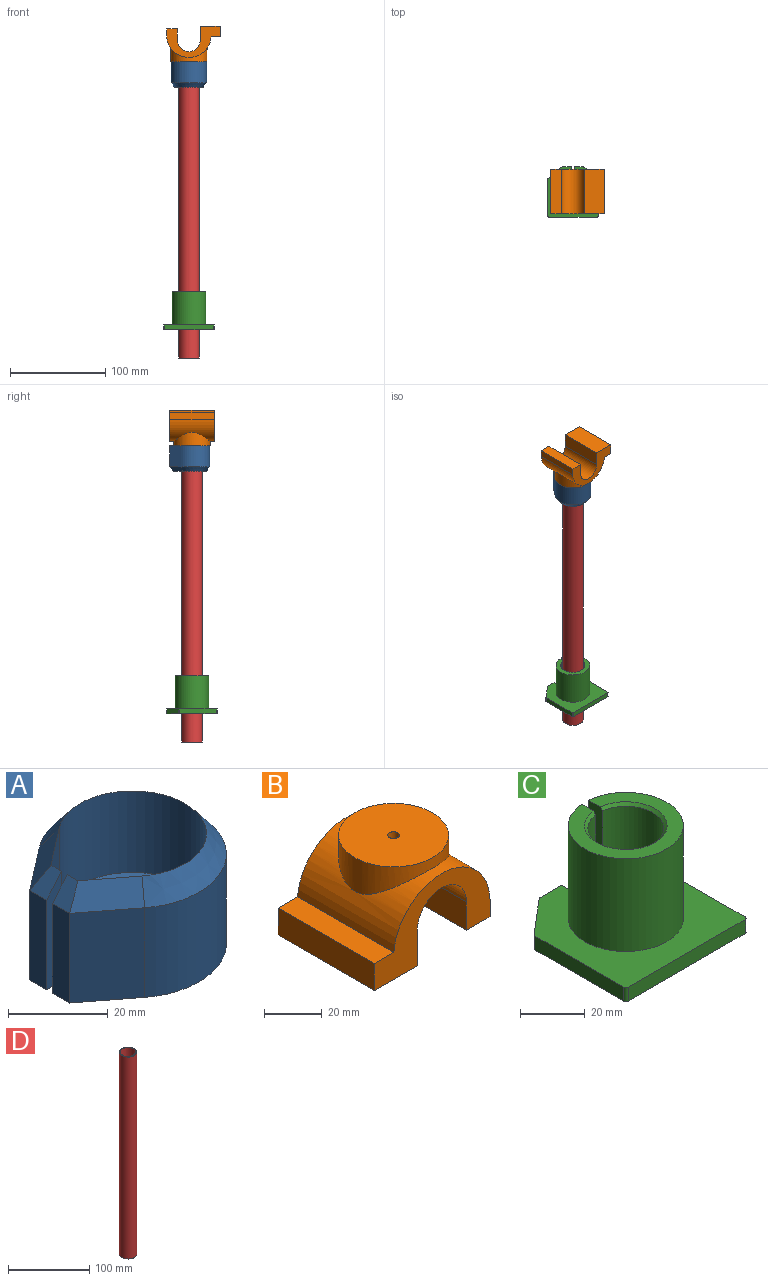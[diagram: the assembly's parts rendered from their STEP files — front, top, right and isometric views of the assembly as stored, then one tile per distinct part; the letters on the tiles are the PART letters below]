
ASSEMBLY  parts=4 mates=3
PART A: 21 faces, bbox 42.3x37.7x27 mm
  f0: plane 27x11.5mm, normal (0,1,0), area 153.9mm2, adj f1,f5,f9,f11,f15,f20
  f1: cylinder r=0.82mm len=7mm, axis (0,0,-1), area 18mm2, adj f0,f4,f9,f20
  f2: cylinder r=2mm len=7mm, axis (0,0,-1), area 88mm2, adj f9,f20
  f3: plane 22x4.83mm, normal (-1,0,0), area 106.3mm2, adj f4,f8,f9,f10
  f4: plane 27x11.5mm, normal (0,-1,0), area 153.9mm2, adj f1,f3,f9,f10,f19,f20
  f5: plane 22x4.86mm, normal (-1,0,0), area 106.9mm2, adj f0,f6,f9,f11
  f6: plane 22x12.01mm, normal (-0.61,-0.79,0), area 333.6mm2, adj f5,f7,f9,f12
  f7: cylinder r=18.83mm len=37.65mm, axis (0,0,-1), area 1844.9mm2, adj f6,f8,f9,f13
  f8: plane 22x12.01mm, normal (-0.61,0.79,0), area 333.6mm2, adj f3,f7,f9,f14
  f9: plane 42.33x37.65mm, normal (0,0,-1), area 1175.4mm2, adj f0,f1,f2,f3,f4,f5,f6,f7
  f10: plane 5x4.83mm, normal (-0.77,0,0.64), area 25.6mm2, adj f3,f4,f14,f19
  f11: plane 5x4.86mm, normal (-0.77,0,0.64), area 25.8mm2, adj f0,f5,f12,f15
  f12: plane 14.45x11.07mm, normal (-0.48,-0.62,0.62), area 90mm2, adj f6,f11,f13,f16
  f13: cone r=14.83mm half-angle=38.7deg, axis (0,0,-1), area 479.9mm2, adj f7,f12,f14,f17
  f14: plane 14.45x11.07mm, normal (-0.48,0.62,0.62), area 90mm2, adj f8,f10,f13,f18
  f15: plane 20x3.04mm, normal (1,0,0), area 60.8mm2, adj f0,f11,f16,f20
  f16: plane 20x10.26mm, normal (0.61,0.79,0), area 258.9mm2, adj f12,f15,f17,f20
  f17: cylinder r=14.83mm len=29.65mm, axis (0,0,1), area 1320.8mm2, adj f13,f16,f18,f20
  f18: plane 20x10.26mm, normal (0.61,-0.79,0), area 258.9mm2, adj f14,f17,f19,f20
  f19: plane 20x3.01mm, normal (1,0,0), area 60.3mm2, adj f4,f10,f18,f20
  f20: plane 34.13x29.65mm, normal (0,0,1), area 730.2mm2, adj f0,f1,f2,f4,f15,f16,f17,f18
PART B: 15 faces, bbox 56.5x47x37.5 mm
  f0: cylinder r=23.51mm len=47mm, axis (0,-1,0), area 2082.5mm2, adj f2,f3,f9,f10,f12
  f1: plane 47x11.5mm, normal (0,0,-1), area 540.5mm2, adj f2,f8,f9,f10
  f2: plane 47x7.3mm, normal (1,0,0), area 343mm2, adj f0,f1,f9,f10
  f3: plane 47x9.56mm, normal (0,0,1), area 449.5mm2, adj f0,f4,f9,f10
  f4: plane 47x11.41mm, normal (-1,0,0), area 536.1mm2, adj f3,f5,f9,f10
  f5: plane 47x21mm, normal (0,0,-1), area 987mm2, adj f4,f6,f9,f10
  f6: plane 47x15mm, normal (1,0,0), area 705mm2, adj f5,f7,f9,f10
  f7: cylinder r=12mm len=47mm, axis (0,-1,0), area 1773.5mm2, adj f6,f8,f9,f10
  f8: plane 47x11.97mm, normal (-1,0,0), area 562.4mm2, adj f1,f7,f9,f10
  f9: plane 56.5x33.02mm, normal (0,1,0), area 802.9mm2, adj f0,f1,f2,f3,f4,f5,f6,f7
  f10: plane 56.5x33.02mm, normal (0,-1,0), area 802.9mm2, adj f0,f1,f2,f3,f4,f5,f6,f7
  f11: plane 38x38mm, normal (0,0,1), area 1121.5mm2, adj f12,f13
  f12: cylinder r=19mm len=38mm, axis (0,0,1), area 1075.4mm2, adj f0,f11
  f13: cylinder r=2mm len=4.57mm, axis (0,0,1), area 56.9mm2, adj f11,f14
  f14: cylinder r=23.51mm len=4mm, axis (0,-1,0), area 12.6mm2, adj f13
PART C: 21 faces, bbox 53x53x40.3 mm
  f0: cylinder r=11.75mm len=39.25mm, axis (0,0,-1), area 2779.7mm2, adj f1,f15,f17,f20
  f1: plane 40.26x14.85mm, normal (1,0,0), area 288.6mm2, adj f0,f2,f16,f17,f18,f19,f20
  f2: plane 9.38x5.25mm, normal (0,1,0), area 49.3mm2, adj f1,f3,f16,f17
  f3: cylinder r=1mm len=5.25mm, axis (0,0,-1), area 3.7mm2, adj f2,f4,f16,f17
  f4: plane 14.62x12.37mm, normal (-0.65,0.76,0), area 100.5mm2, adj f3,f5,f16,f17
  f5: cylinder r=1mm len=5.25mm, axis (0,0,-1), area 4.6mm2, adj f4,f6,f16,f17
  f6: plane 38.62x5.25mm, normal (-1,0,0), area 202.7mm2, adj f5,f7,f16,f17
  f7: cylinder r=1mm len=5.25mm, axis (0,0,-1), area 8.2mm2, adj f6,f8,f16,f17
  f8: plane 51x5.25mm, normal (0,-1,0), area 267.8mm2, adj f7,f9,f16,f17
  f9: cylinder r=1mm len=5.25mm, axis (0,0,-1), area 8.2mm2, adj f8,f10,f16,f17
  f10: plane 38.62x5.25mm, normal (1,0,0), area 202.7mm2, adj f9,f11,f16,f17
  f11: cylinder r=1mm len=5.25mm, axis (0,0,-1), area 4.6mm2, adj f10,f12,f16,f17
  f12: plane 14.62x12.37mm, normal (0.65,0.76,0), area 100.5mm2, adj f11,f13,f16,f17
  f13: cylinder r=1mm len=5.25mm, axis (0,0,-1), area 3.7mm2, adj f12,f14,f16,f17
  f14: plane 9.38x5.25mm, normal (0,1,0), area 49.3mm2, adj f13,f15,f16,f17
  f15: plane 40.26x14.85mm, normal (-1,0,0), area 288.6mm2, adj f0,f14,f16,f17,f18,f19,f20
  f16: plane 53x52.99mm, normal (0,0,1), area 1594.9mm2, adj f1,f2,f3,f4,f5,f6,f7,f8
  f17: plane 53x52.99mm, normal (0,0,-1), area 2132.9mm2, adj f0,f1,f2,f3,f4,f5,f6,f7
  f18: cylinder r=17.75mm len=35.5mm, axis (0,0,-1), area 3798.3mm2, adj f1,f15,f16,f19
  f19: plane 35.5x35.44mm, normal (0,0,1), area 464.1mm2, adj f1,f15,f18,f20
  f20: cone r=11.75mm half-angle=45deg, axis (0,0,1), area 104.6mm2, adj f0,f1,f15,f19
PART D: 4 faces, bbox 21.5x21.5x304.8 mm
  f0: cylinder r=9.53mm len=304.8mm, axis (0,0,-1), area 18241.5mm2, adj f2,f3
  f1: cylinder r=10.77mm len=304.8mm, axis (0,0,-1), area 20625mm2, adj f2,f3
  f2: plane 21.54x21.54mm, normal (0,0,1), area 79.4mm2, adj f0,f1
  f3: plane 21.54x21.54mm, normal (0,0,-1), area 79.4mm2, adj f0,f1
PLACE A rot(axis=(0.71,-0.71,0),180deg) t=(0,2.3,248.65)mm
PLACE B rot(axis=(0,1,0),180deg) t=(4.92,0,279.65)mm
PLACE C at identity fixed
PLACE D t=(0,0,-49.65)mm
MATE fastened A.f2 <-> B.f12  axis (0,0,1) through (0,0,262.15)mm
MATE fastened A.f2 <-> D.f0  axis (0,0,-1) through (0,0,255.15)mm
MATE slider D.f0 <-> C.f0  axis (0,0,-1) through (0,0,102.75)mm
